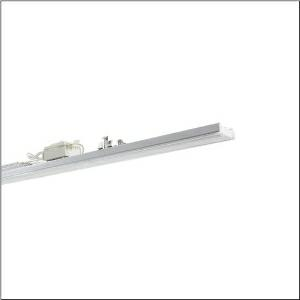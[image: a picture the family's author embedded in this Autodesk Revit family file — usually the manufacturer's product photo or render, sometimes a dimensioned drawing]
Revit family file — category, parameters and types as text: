
# Revit family: licross_r__21_recessed_mo_52tl147n48xg_d69c
name_source: partatom
category: Lighting Fixtures
units: mm (PartAtom-declared; Revit-internal decimal feet)

## family parameters
Cut with Voids When Loaded = No
Host = Face
Light Source = No
Part Type = Normal
Room Calculation Point = No
Round Connector Dimension = Use Diameter
Shared = No

## types (1)
- Licross® 21 Recessed MO (1 x LED, 8120 lm, 47.9 W, 4000K)
    Apparent Load = 48 VA
    CIE Flux Codes = 56 84 97 100 100
    Color Rendering = 80
    Color Temperature = 4000K
    Default Elevation = 1800 mm
    Description = Licross® 21 Recessed MO, luminaire insert, of sheet steel, galvanised, coil coated, white, length: 1.500mm, width: 66mm, height: 67mm, LED rated luminous flux: 8.120lm, light colour: 840, control gear: ON/OFF, with plug, 3-pole, with phase selection, mains connection: 220..240V, AC, 50/60Hz, rated input power: 48W, internal wiring halogen-free, primary light control with lens, of plastic, primary optical cover: cover, of PMMA, light emission: direct distribution, primary light characteristic: asymmetric, protection rating (complete): IP40, insulation class (complete): insulation class I (protective earthing), certification: CE, ENEC, VDE, UKCA, protection symbol: D if used in an environment without relevant dust loads with corresponding accessories, impact resistance: IK06, permissible ambient temperature for indoor applications: -35..+40°C, corresponds to IFS (International Featured Standards) requirements for safety and quality in the food industry, reducing of maximum allowable ambient temperature of 5°C with ceiling mounting, LABS conformity tested according to VDMA 24364:2018-05, packaging unit: 1 piece
    Height = 58 mm
    Lamp = 1 x LED
    Lamp Light Flux = 8120 lm
    Lamp Power = 47.9 W
    Lamp count = 1
    Length = 1500 mm
    Luminous efficacy = 170 lm/W
    Manufacturer = Siteco
    ModVariant = No
    Model = 52TL147N48XG
    Mounting Place = Ceiling
    Mounting Type = Pendant
    Number of Poles = 1
    OnlyDefault = Yes
    Power Factor = 1
    Product Name = Licross® 21 Recessed MO
    Product group = luminaire insert | ceiling pendant
    ProductGroupID = 902
    Protection Class = Protection class I
    Protection Degree = IP 40
    RLX_Detail_Level = 1
    RLX_Emergency_Light_Flux = 0 lm
    RLX_Emergency_Type = 0
    RLX_Emergency_Type_DB = No
    RlxData = <blob elided: 21385 chars, md5=19c7a5b4>
    Socket = socket
    Standby Power = 0 W
    System Light Flux = 8120 lm
    System Power = 48 W
    Type Comments = Product without accessories
    Type Image = l_1296930.jpg
    URL = http://relux.com
    VarID = ---
    Voltage = 0 V
    Weight = 0.00 kg
    Width = 66 mm

## geometry (parser evidence)
native form markers: Blend x4, Sweep x12
no freeform markers — native parametric forms only
